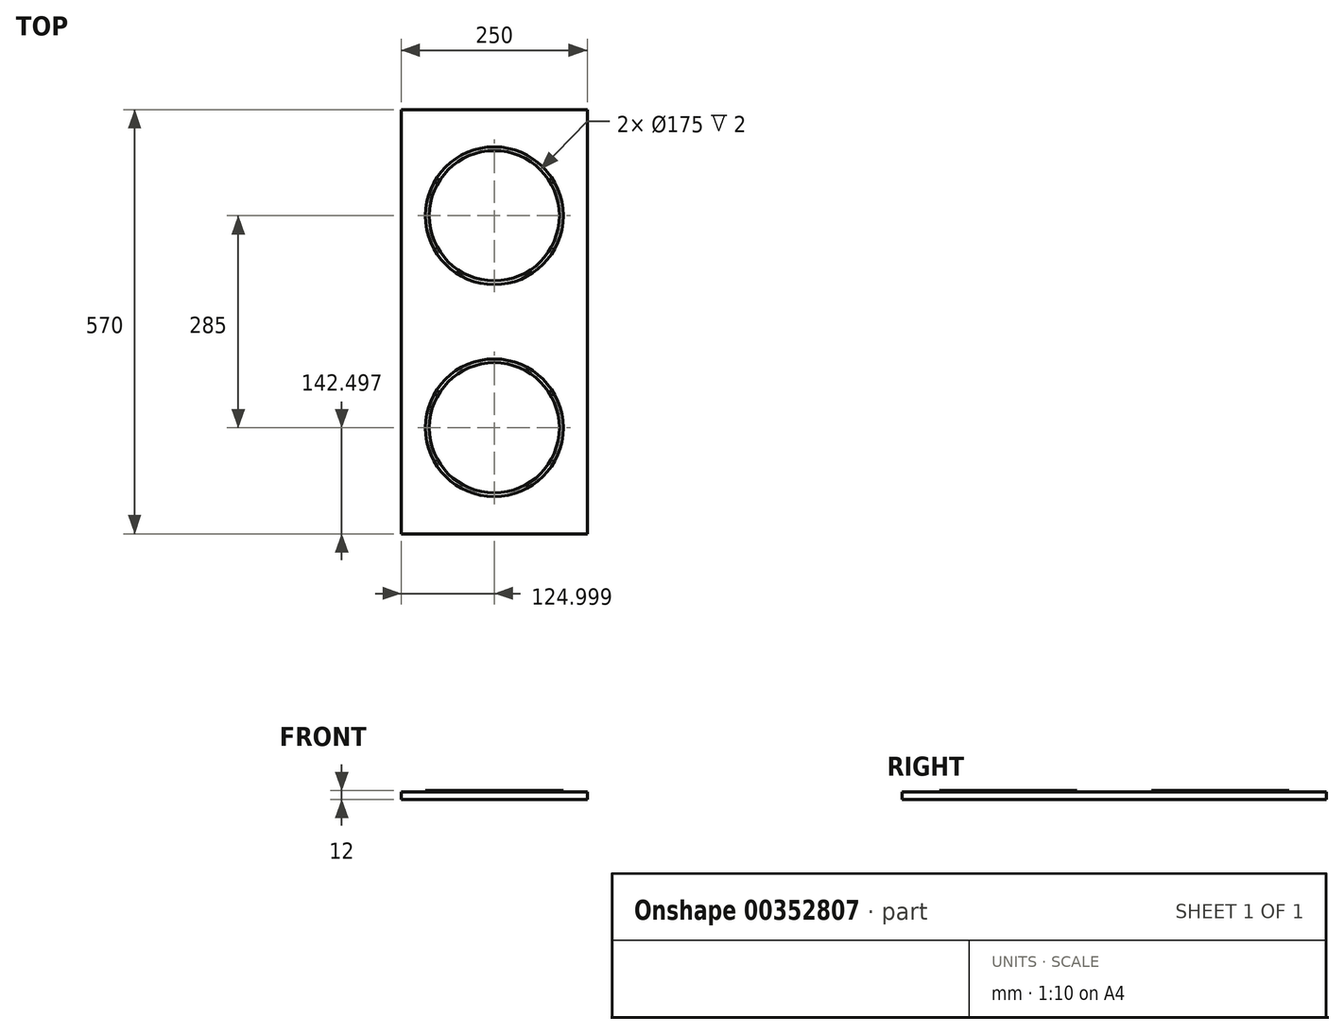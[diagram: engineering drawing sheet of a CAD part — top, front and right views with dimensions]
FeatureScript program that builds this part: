
annotation { "Feature Type Name" : "Feature", "Feature Type Description" : "" }
export const myFeature = defineFeature(function(context is Context, id is Id, definition is map)
    precondition{}
    {
        {
            var Q0;
            Q0=qCreatedBy(makeId("Top.planeOp"),FACE);
            var sketch = newSketch(context, id + "F0", { "sketchPlane" : qUnion([Q0])});
            skLineSegment(sketch, "E0.bottom", {"start": v(-11.84, 533) * mm, "end": v(238.16, 533) * mm});
            skLineSegment(sketch, "E0.top", {"start": v(-11.84, -37) * mm, "end": v(238.16, -37) * mm});
            skLineSegment(sketch, "E0.left", {"start": v(-11.84, 533) * mm, "end": v(-11.84, -37) * mm});
            skLineSegment(sketch, "E0.right", {"start": v(238.16, 533) * mm, "end": v(238.16, -37) * mm});
            skSolve(sketch);
        }
        {
            var Q0;
            Q0 = qSketchRegion(id + "F0", true);
            extrude(context, id + "F1", {"entities" : qUnion([Q0]), "depth" : 10 * mm});
        }
        {
            var Q0;
            Q0=makeQuery(id+"F1.opExtrude","CAP_FACE",FACE,{"disambiguationData":[OSD([sQuery(id+"F0.wireOp",EDGE,"E0.bottom"),sQuery(id+"F0.wireOp",EDGE,"E0.top"),sQuery(id+"F0.wireOp",EDGE,"E0.left"),sQuery(id+"F0.wireOp",EDGE,"E0.right")])],"isStart":false});
            var sketch = newSketch(context, id + "F2", { "sketchPlane" : qUnion([Q0])});
            skLineSegment(sketch, "E1", {"start": v(238.16, 248) * mm, "end": v(-11.84, 248) * mm});
            skLineSegment(sketch, "E2", {"start": v(-11.84, 248) * mm, "end": v(238.16, 533) * mm});
            skLineSegment(sketch, "E3", {"start": v(238.16, 248) * mm, "end": v(-11.84, -37) * mm});
            skCircle(sketch, "E4", {"center": v(113.16, 390.5) * mm, "radius": 87.5 * mm});
            skCircle(sketch, "E5", {"center": v(113.16, 105.5) * mm, "radius": 87.5 * mm});
            skCircle(sketch, "E6.0", {"center": v(113.16, 390.5) * mm, "radius": 92.5 * mm});
            skCircle(sketch, "E7.0", {"center": v(113.16, 105.5) * mm, "radius": 92.5 * mm});
            skSolve(sketch);
        }
        {
            var Q0;
            Q0 = qSketchRegion(id + "F2", true);
            extrude(context, id + "F3", {"entities" : qUnion([Q0]), "operationType" : NewBodyOperationType.ADD, "depth" : 2 * mm});
        }
    });
